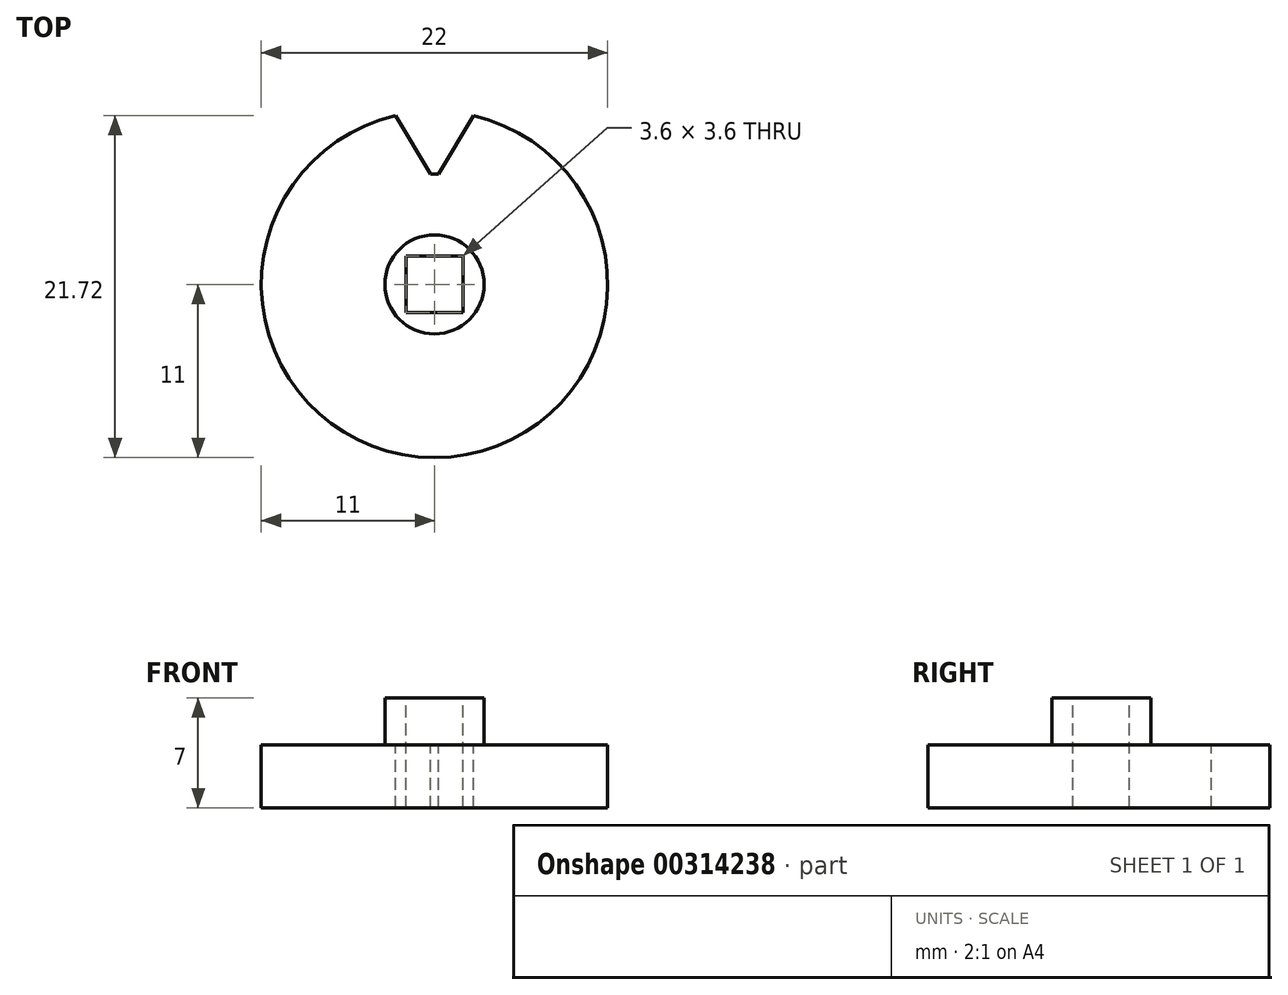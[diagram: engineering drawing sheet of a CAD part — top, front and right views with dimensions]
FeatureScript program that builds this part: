
annotation { "Feature Type Name" : "Feature", "Feature Type Description" : "" }
export const myFeature = defineFeature(function(context is Context, id is Id, definition is map)
    precondition{}
    {
        {
            var Q0;
            Q0=qCreatedBy(makeId("Top.planeOp"),FACE);
            var sketch = newSketch(context, id + "F0", { "sketchPlane" : qUnion([Q0])});
            skCircle(sketch, "E0", {"center": v(0, 0) * mm, "radius": 11 * mm});
            skSolve(sketch);
        }
        {
            var Q0;
            Q0 = qSketchRegion(id + "F0", true);
            extrude(context, id + "F1", {"entities" : qUnion([Q0]), "depth" : 4 * mm});
        }
        {
            var Q0;
            Q0=makeQuery(id+"F1.opExtrude","CAP_FACE",FACE,{"disambiguationData":[OSD([sQuery(id+"F0.wireOp",EDGE,"E0")])],"isStart":false});
            var sketch = newSketch(context, id + "F2", { "sketchPlane" : qUnion([Q0])});
            skLineSegment(sketch, "E1", {"start": v(0, 0) * mm, "end": v(0, 11) * mm});
            skLineSegment(sketch, "E2", {"start": v(0, 0) * mm, "end": v(0.24, 7) * mm});
            skLineSegment(sketch, "E3", {"start": v(0, 0) * mm, "end": v(2.47, 10.72) * mm});
            skLineSegment(sketch, "E4.MirrorCS", {"start": v(0, 0) * mm, "end": v(-0.24, 7) * mm});
            skLineSegment(sketch, "E5.MirrorCS", {"start": v(0, 0) * mm, "end": v(-2.47, 10.72) * mm});
            skArc(sketch, "E6", {"start": v(-0.24, 7) * mm, "mid": v(0, 7) * mm, "end": v(0.24, 7) * mm});
            skLineSegment(sketch, "E7", {"start": v(-2.47, 10.72) * mm, "end": v(-0.24, 7) * mm});
            skLineSegment(sketch, "E8", {"start": v(0.24, 7) * mm, "end": v(2.47, 10.72) * mm});
            skSolve(sketch);
        }
        {
            var Q0;
            {var subQ5=sQuery(id+"F2.wireOp",EDGE,"E7");Q0=makeQuery(id+"F2.imprint","IMPRINT",FACE,{"disambiguationData":[TD([[makeQuery(id+"F2.imprint","IMPRINT",EDGE,{"derivedFrom":subQ5}),1.0]])]});}
            var Q1;
            {var subQ5=sQuery(id+"F2.wireOp",EDGE,"E8");Q1=makeQuery(id+"F2.imprint","IMPRINT",FACE,{"disambiguationData":[TD([[makeQuery(id+"F2.imprint","IMPRINT",EDGE,{"derivedFrom":subQ5}),1.0]])]});}
            extrude(context, id + "F3", {"entities" : qUnion([Q0, Q1]), "operationType" : NewBodyOperationType.REMOVE, "endBound" : BoundingType.THROUGH_ALL, "oppositeDirection" : true, "depth" : 25 * mm});
        }
        {
            var Q0;
            Q0=qCreatedBy(makeId("Front.planeOp"),FACE);
            var sketch = newSketch(context, id + "F4", { "sketchPlane" : qUnion([Q0])});
            skLineSegment(sketch, "E9", {"start": v(0, 0) * mm, "end": v(0, -5.93) * mm});
            skSolve(sketch);
        }
        {
            var Q0;
            Q0=makeQuery(id+"F1.opExtrude","CAP_FACE",FACE,{"disambiguationData":[OSD([sQuery(id+"F0.wireOp",EDGE,"E0")])],"isStart":false});
            var sketch = newSketch(context, id + "F5", { "sketchPlane" : qUnion([Q0])});
            skCircle(sketch, "E10", {"center": v(0, 0) * mm, "radius": 3.15 * mm});
            skSolve(sketch);
        }
        {
            var Q0;
            Q0 = qSketchRegion(id + "F5", true);
            extrude(context, id + "F6", {"entities" : qUnion([Q0]), "operationType" : NewBodyOperationType.ADD, "depth" : 3 * mm});
        }
        {
            var Q0;
            Q0=makeQuery(id+"F6.opExtrude","CAP_FACE",FACE,{"disambiguationData":[OSD([sQuery(id+"F5.wireOp",EDGE,"E10")])],"isStart":false});
            var sketch = newSketch(context, id + "F7", { "sketchPlane" : qUnion([Q0])});
            skLineSegment(sketch, "E11.bottom", {"start": v(1.8, 1.8) * mm, "end": v(-1.8, 1.8) * mm});
            skLineSegment(sketch, "E11.top", {"start": v(1.8, -1.8) * mm, "end": v(-1.8, -1.8) * mm});
            skLineSegment(sketch, "E11.left", {"start": v(1.8, 1.8) * mm, "end": v(1.8, -1.8) * mm});
            skLineSegment(sketch, "E11.right", {"start": v(-1.8, 1.8) * mm, "end": v(-1.8, -1.8) * mm});
            skPoint(sketch, "E11.middle", {"position": v(0, 0) * mm});
            skSolve(sketch);
        }
        {
            var Q0;
            Q0 = qSketchRegion(id + "F7", true);
            extrude(context, id + "F8", {"entities" : qUnion([Q0]), "operationType" : NewBodyOperationType.REMOVE, "endBound" : BoundingType.UP_TO_NEXT, "oppositeDirection" : true, "depth" : 25 * mm});
        }
    });
